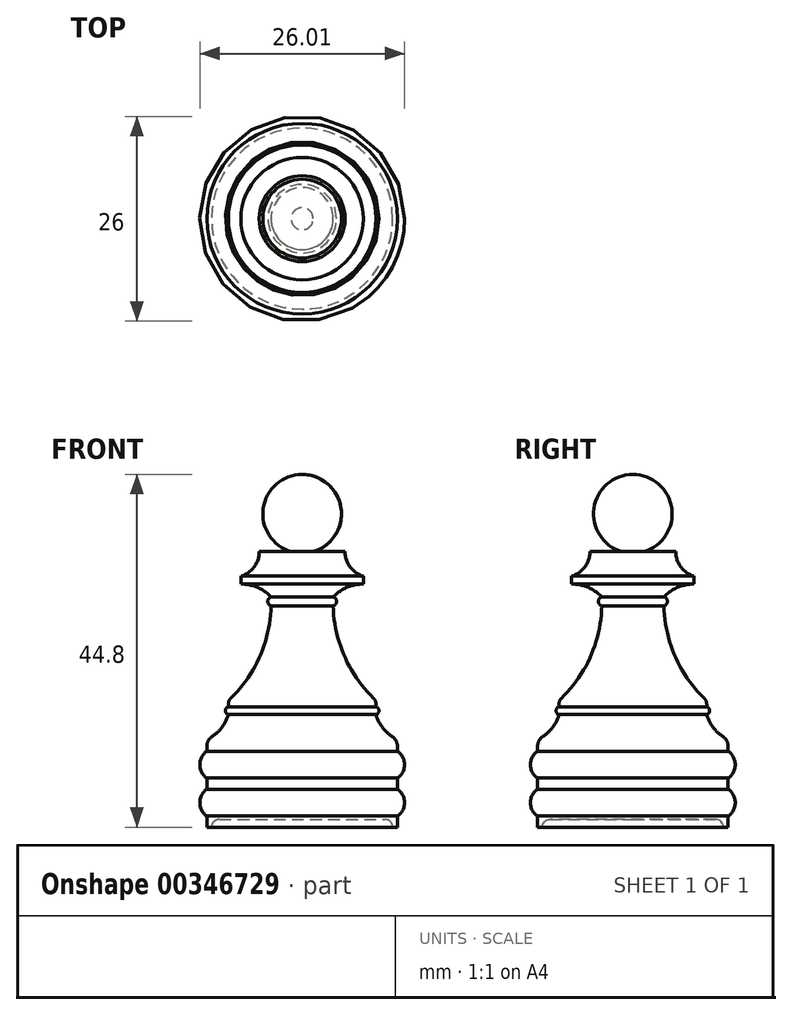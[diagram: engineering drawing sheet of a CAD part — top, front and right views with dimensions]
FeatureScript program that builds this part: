
annotation { "Feature Type Name" : "Feature", "Feature Type Description" : "" }
export const myFeature = defineFeature(function(context is Context, id is Id, definition is map)
    precondition{}
    {
        {
            var Q0;
            Q0=qCreatedBy(makeId("Front.planeOp"),FACE);
            var sketch = newSketch(context, id + "F0", { "sketchPlane" : qUnion([Q0])});
            skLineSegment(sketch, "E0", {"start": v(-277.8, 59.26) * mm, "end": v(-277.8, 24.26) * mm});
            skLineSegment(sketch, "E1", {"start": v(-277.8, 24.26) * mm, "end": v(-265.7, 24.26) * mm});
            skLineSegment(sketch, "E2", {"start": v(-265.7, 24.26) * mm, "end": v(-265.7, 25.67) * mm});
            skLineSegment(sketch, "E3", {"start": v(-272.35, 59.26) * mm, "end": v(-272.35, 56.14) * mm});
            skLineSegment(sketch, "E4", {"start": v(-272.35, 56.14) * mm, "end": v(-270.03, 56.14) * mm});
            skLineSegment(sketch, "E5", {"start": v(-270.03, 56.14) * mm, "end": v(-270.03, 55.14) * mm});
            skLineSegment(sketch, "E6", {"start": v(-270.03, 55.14) * mm, "end": v(-273.86, 55.14) * mm});
            skLineSegment(sketch, "E7", {"start": v(-273.86, 55.14) * mm, "end": v(-273.86, 53.51) * mm});
            skArc(sketch, "E8", {"start": v(-273.86, 52.36) * mm, "mid": v(-273.42, 52.94) * mm, "end": v(-273.86, 53.51) * mm});
            skLineSegment(sketch, "E9", {"start": v(-273.86, 52.36) * mm, "end": v(-273.86, 40.9) * mm});
            skLineSegment(sketch, "E10", {"start": v(-273.86, 40.9) * mm, "end": v(-268.42, 40.9) * mm});
            skLineSegment(sketch, "E11", {"start": v(-268.42, 40.9) * mm, "end": v(-268.42, 39.56) * mm});
            skArc(sketch, "E12", {"start": v(-268.42, 38.56) * mm, "mid": v(-268.05, 39.06) * mm, "end": v(-268.42, 39.56) * mm});
            skLineSegment(sketch, "E13", {"start": v(-268.42, 38.56) * mm, "end": v(-268.42, 36.04) * mm});
            skArc(sketch, "E14", {"start": v(-265.7, 25.67) * mm, "mid": v(-264.8, 27.37) * mm, "end": v(-265.7, 29.08) * mm});
            skLineSegment(sketch, "E15", {"start": v(-265.7, 29.08) * mm, "end": v(-265.7, 30.49) * mm});
            skArc(sketch, "E16", {"start": v(-265.7, 30.49) * mm, "mid": v(-264.8, 32.2) * mm, "end": v(-265.7, 33.9) * mm});
            skLineSegment(sketch, "E17", {"start": v(-265.7, 33.9) * mm, "end": v(-265.7, 36.04) * mm});
            skLineSegment(sketch, "E18", {"start": v(-265.7, 36.04) * mm, "end": v(-268.42, 36.04) * mm});
            skLineSegment(sketch, "E19", {"start": v(-277.8, 59.26) * mm, "end": v(-277.8, 69.06) * mm});
            skPoint(sketch, "E20", {"position": v(-277.8, 59.06) * mm});
            skArc(sketch, "E21", {"start": v(-277.8, 59.06) * mm, "mid": v(-272.8, 64.06) * mm, "end": v(-277.8, 69.06) * mm});
            skLineSegment(sketch, "E22", {"start": v(-272.35, 59.26) * mm, "end": v(-276.4, 59.26) * mm});
            skSolve(sketch);
        }
        {
            var Q0;
            Q0=makeQuery(id+"F0.imprint","IMPRINT",FACE,{"disambiguationData":[TD([[makeQuery(id+"F0.imprint","IMPRINT",EDGE,{"derivedFrom":sQuery(id+"F0.wireOp",EDGE,"E0")}),1.0]])]});
            var Q1;
            {var subQ0=sQuery(id+"F0.wireOp",EDGE,"E1");Q1=makeQuery(id+"F0.imprint","IMPRINT",FACE,{"disambiguationData":[TD([[makeQuery(id+"F0.imprint","IMPRINT",EDGE,{"derivedFrom":subQ0}),1.0]])]});}
            var Q2;
            Q2=sQuery(id+"F0.wireOp",EDGE,"E0");
            revolve(context, id + "F1", {"entities" : qUnion([Q0, Q1]), "axis" : qUnion([Q2]), "revolveType" : RevolveType.FULL});
        }
        {
            var Q0;
            Q0=makeQuery(id+"F1.opRevolve","SWEPT_EDGE",EDGE,{"disambiguationData":[OSD([sQuery(id+"F0.wireOp",EDGE,"E17"),sQuery(id+"F0.wireOp",EDGE,"E18")])]});
            fillet(context, id + "F2", {"entities" : qUnion([Q0]), "radius" : 1.5 * mm, "tangentPropagation" : true, "allowEdgeOverflow" : false});
        }
        {
            var Q0;
            Q0=makeQuery(id+"F1.opRevolve","SWEPT_EDGE",EDGE,{"disambiguationData":[OSD([sQuery(id+"F0.wireOp",EDGE,"E13"),sQuery(id+"F0.wireOp",EDGE,"E18")])]});
            fillet(context, id + "F3", {"entities" : qUnion([Q0]), "radius" : 5 * mm, "tangentPropagation" : true, "allowEdgeOverflow" : false});
        }
        {
            var Q0;
            Q0=makeQuery(id+"F1.opRevolve","SWEPT_EDGE",EDGE,{"disambiguationData":[OSD([sQuery(id+"F0.wireOp",EDGE,"E10"),sQuery(id+"F0.wireOp",EDGE,"E11")])]});
            fillet(context, id + "F4", {"entities" : qUnion([Q0]), "radius" : 1 * mm, "tangentPropagation" : true, "allowEdgeOverflow" : false});
        }
        {
            var Q0;
            Q0=makeQuery(id+"F1.opRevolve","SWEPT_EDGE",EDGE,{"disambiguationData":[OSD([sQuery(id+"F0.wireOp",EDGE,"E9"),sQuery(id+"F0.wireOp",EDGE,"E10")])]});
            fillet(context, id + "F5", {"entities" : qUnion([Q0]), "radius" : 17 * mm, "tangentPropagation" : true, "allowEdgeOverflow" : false});
        }
        {
            var Q0;
            Q0=makeQuery(id+"F1.opRevolve","SWEPT_EDGE",EDGE,{"disambiguationData":[OSD([sQuery(id+"F0.wireOp",EDGE,"E6"),sQuery(id+"F0.wireOp",EDGE,"E7")])]});
            fillet(context, id + "F6", {"entities" : qUnion([Q0]), "radius" : 5.3 * mm, "tangentPropagation" : true, "allowEdgeOverflow" : false});
        }
        {
            var Q0;
            Q0=makeQuery(id+"F1.opRevolve","SWEPT_EDGE",EDGE,{"disambiguationData":[OSD([sQuery(id+"F0.wireOp",EDGE,"E3"),sQuery(id+"F0.wireOp",EDGE,"E4")])]});
            fillet(context, id + "F7", {"entities" : qUnion([Q0]), "radius" : 3.25 * mm, "tangentPropagation" : true, "allowEdgeOverflow" : false});
        }
        {
            var Q0;
            Q0=makeQuery(id+"F1.opRevolve","SWEPT_FACE",FACE,{"disambiguationData":[OSD([sQuery(id+"F0.wireOp",EDGE,"E1")])]});
            var sketch = newSketch(context, id + "F8", { "sketchPlane" : qUnion([Q0])});
            skCircle(sketch, "E23", {"center": v(-277.8, 0) * mm, "radius": 11.5 * mm});
            skSolve(sketch);
        }
        {
            var Q0;
            Q0=makeQuery(id+"F8.imprint","IMPRINT",FACE,{"disambiguationData":[TD([[makeQuery(id+"F8.imprint","IMPRINT",EDGE,{"derivedFrom":sQuery(id+"F8.wireOp",EDGE,"E23")}),1.0]])]});
            extrude(context, id + "F9", {"entities" : qUnion([Q0]), "operationType" : NewBodyOperationType.REMOVE, "oppositeDirection" : true, "depth" : 1 * mm});
        }
        {
            var Q0;
            Q0=makeQuery(id+"F9.boolean.opBoolean","COPY",EDGE,{"derivedFrom":makeQuery(id+"F9.opExtrude","CAP_EDGE",EDGE,{"disambiguationData":[OSD([sQuery(id+"F8.wireOp",EDGE,"E23")])],"isStart":false})});
            fillet(context, id + "F10", {"entities" : qUnion([Q0]), "radius" : 1 * mm, "tangentPropagation" : true, "allowEdgeOverflow" : false});
        }
    });
